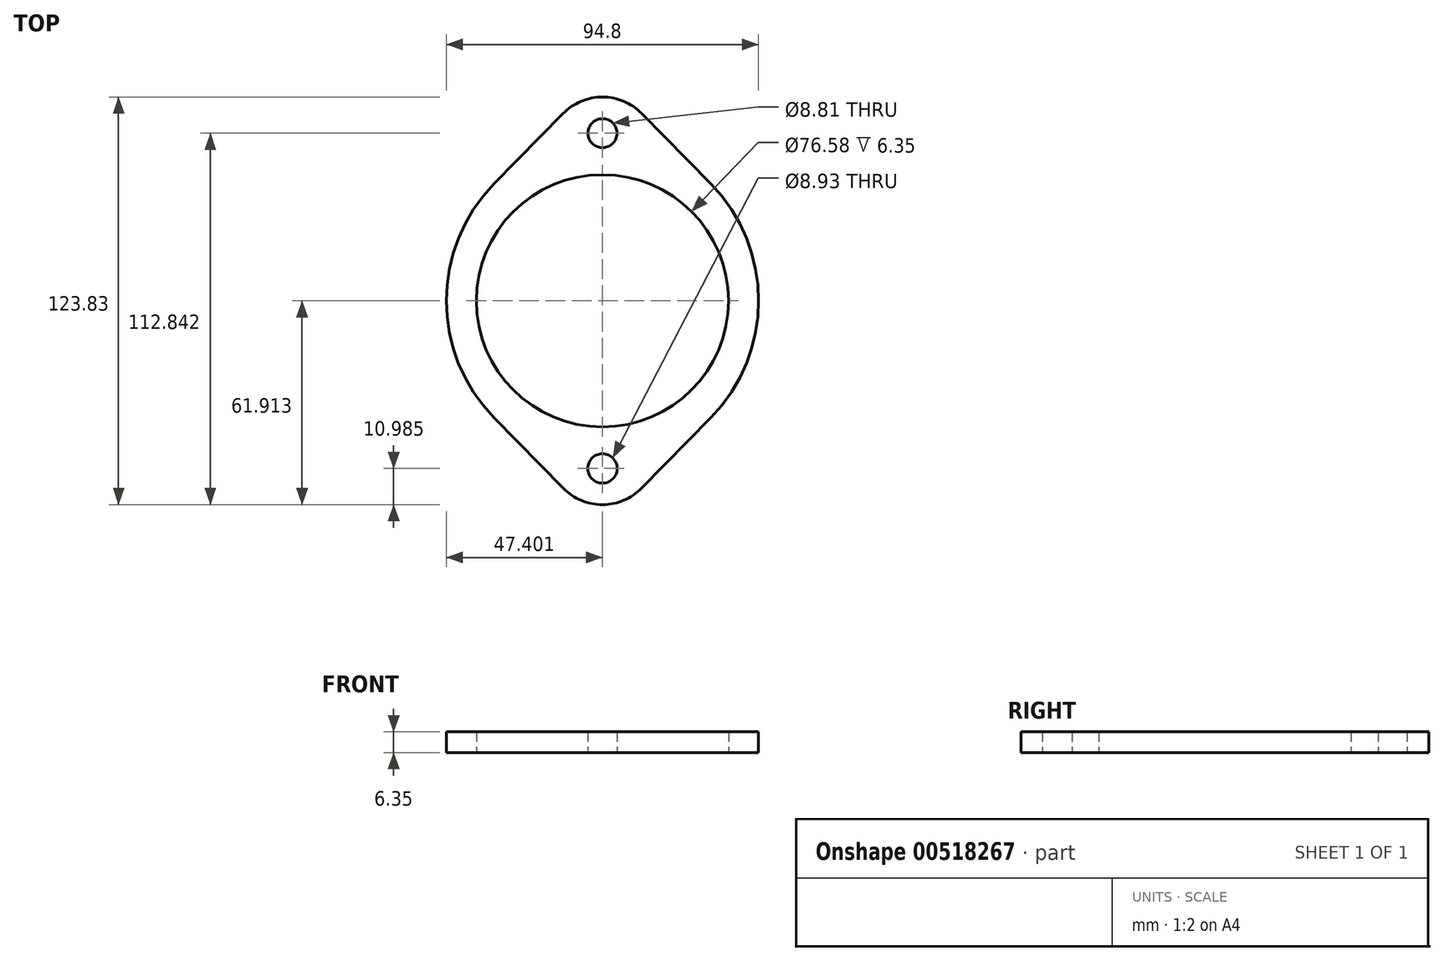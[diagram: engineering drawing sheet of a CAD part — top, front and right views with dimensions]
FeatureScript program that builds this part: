
annotation { "Feature Type Name" : "Feature", "Feature Type Description" : "" }
export const myFeature = defineFeature(function(context is Context, id is Id, definition is map)
    precondition{}
    {
        {
            var Q0;
            Q0=qCreatedBy(makeId("Top.planeOp"),FACE);
            var sketch = newSketch(context, id + "F0", { "sketchPlane" : qUnion([Q0])});
            skLineSegment(sketch, "E0", {"start": v(-11.45, 51.22) * mm, "end": v(-32.38, 29.92) * mm});
            skLineSegment(sketch, "E1", {"start": v(-32.4, -41.25) * mm, "end": v(-11.46, -62.59) * mm});
            skLineSegment(sketch, "E2", {"start": v(12.4, -62.59) * mm, "end": v(33.34, -41.25) * mm});
            skLineSegment(sketch, "E3", {"start": v(33.32, 29.92) * mm, "end": v(12.4, 51.22) * mm});
            skPoint(sketch, "E4.visualSharp", {"position": v(0.47, 63.37) * mm});
            skArc(sketch, "E4.filletArc", {"start": v(5.03, 58.73) * mm, "mid": v(5.01, 58.74) * mm, "end": v(5, 58.75) * mm});
            skPoint(sketch, "E5.visualSharp", {"position": v(-67.3, -5.66) * mm});
            skPoint(sketch, "E6.visualSharp", {"position": v(68.25, -5.66) * mm});
            skPoint(sketch, "E7.visualSharp", {"position": v(0.47, -74.75) * mm});
            skPoint(sketch, "E8.newPointB", {"position": v(-64.42, -8.6) * mm});
            skPoint(sketch, "E5.filletArc.start.orphan", {"position": v(-55.7, 2.72) * mm});
            skPoint(sketch, "E9.newPointB", {"position": v(58.37, -15.73) * mm});
            skPoint(sketch, "E6.filletArc.end.orphan", {"position": v(58.96, 4.95) * mm});
            skCircle(sketch, "E10", {"center": v(0.47, 45.24) * mm, "radius": 4.4 * mm});
            skCircle(sketch, "E11.MirrorC", {"center": v(0.47, -56.62) * mm, "radius": 4.47 * mm});
            skArc(sketch, "E12.filletArc", {"start": v(-32.38, 29.92) * mm, "mid": v(-46.93, -5.66) * mm, "end": v(-32.4, -41.25) * mm});
            skArc(sketch, "E13.filletArc", {"start": v(33.34, -41.25) * mm, "mid": v(47.87, -5.66) * mm, "end": v(33.32, 29.92) * mm});
            skArc(sketch, "E14.filletArc", {"start": v(12.4, 51.22) * mm, "mid": v(0.47, 56.23) * mm, "end": v(-11.45, 51.22) * mm});
            skPoint(sketch, "E15.newPointA", {"position": v(-11.06, -63) * mm});
            skPoint(sketch, "E15.newPointB", {"position": v(5, -70.13) * mm});
            skArc(sketch, "E15.filletArc", {"start": v(-11.46, -62.59) * mm, "mid": v(0.47, -67.6) * mm, "end": v(12.4, -62.59) * mm});
            skPoint(sketch, "E16.filletArc.end.orphan", {"position": v(-4.06, 58.75) * mm});
            skPoint(sketch, "E16.filletArc.start.orphan", {"position": v(5, 58.75) * mm});
            skArc(sketch, "E17.trimOffspring", {"start": v(-4.06, 58.75) * mm, "mid": v(-4.16, 58.65) * mm, "end": v(-4.26, 58.54) * mm});
            skCircle(sketch, "E18", {"center": v(0.47, -5.69) * mm, "radius": 38.29 * mm});
            skLineSegment(sketch, "E19.trimOffspring", {"start": v(0.47, -50.88) * mm, "end": v(0.47, -56.62) * mm});
            skSolve(sketch);
        }
        {
            var Q0;
            Q0=makeQuery(id+"F0.imprint","IMPRINT",FACE,{"disambiguationData":[TD([[makeQuery(id+"F0.imprint","IMPRINT",EDGE,{"derivedFrom":sQuery(id+"F0.wireOp",EDGE,"E0")}),1.0]])]});
            extrude(context, id + "F1", {"entities" : qUnion([Q0]), "depth" : 6.35 * mm, "offsetDistance" : 25.4 * mm});
        }
    });
